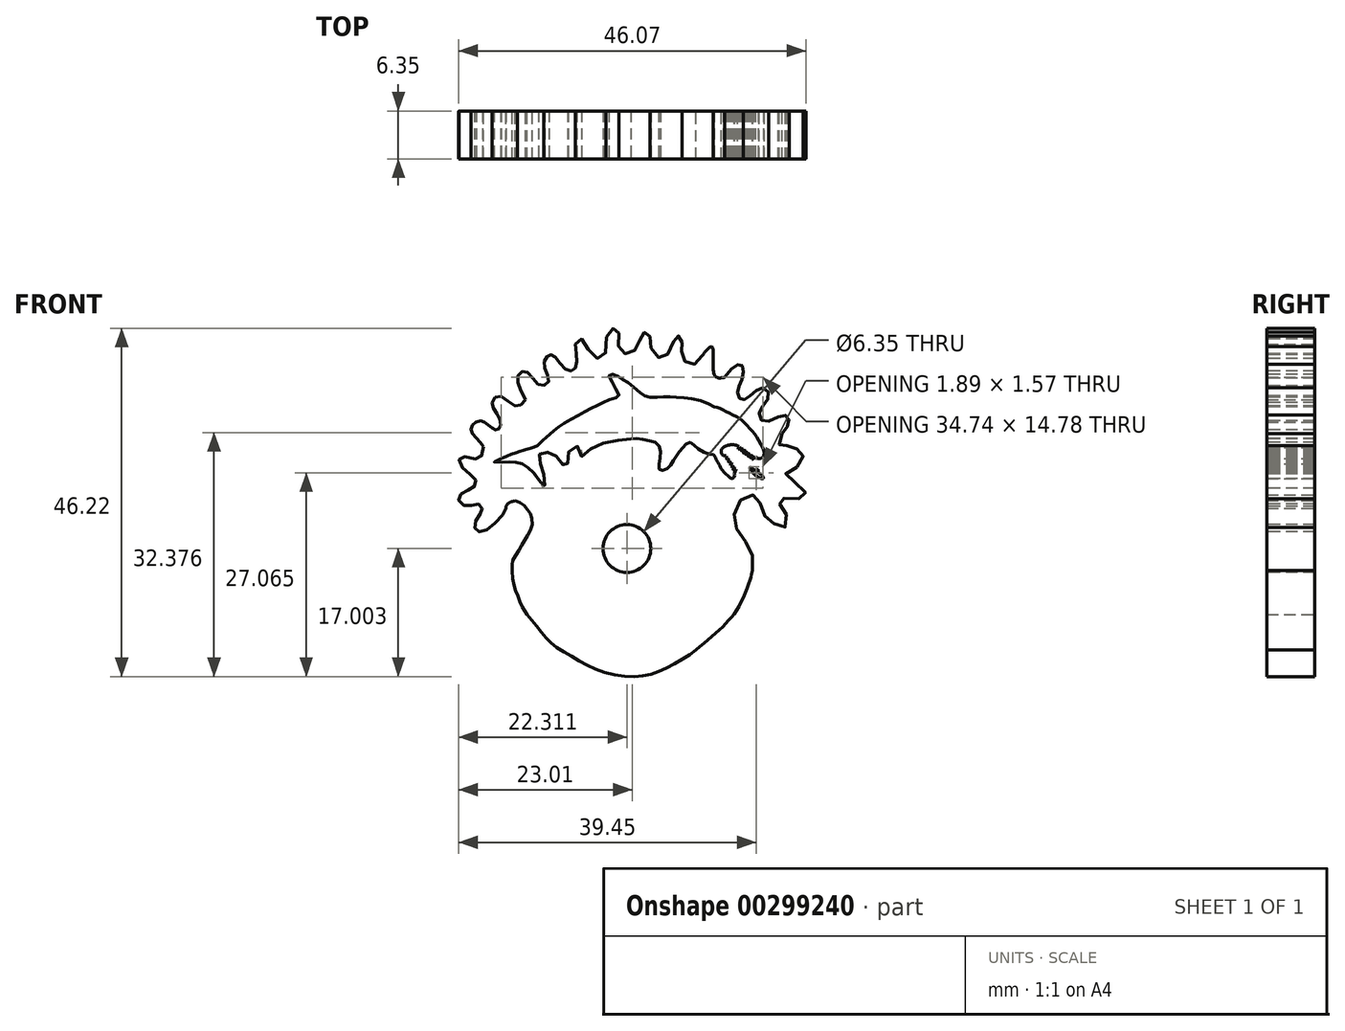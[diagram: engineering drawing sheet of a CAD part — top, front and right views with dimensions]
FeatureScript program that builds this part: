
annotation { "Feature Type Name" : "Feature", "Feature Type Description" : "" }
export const myFeature = defineFeature(function(context is Context, id is Id, definition is map)
    precondition{}
    {
        {
            var Q0;
            Q0=qCreatedBy(makeId("Front.planeOp"),FACE);
            var sketch = newSketch(context, id + "F0", { "sketchPlane" : qUnion([Q0])});
            skFitSpline(sketch, "E0", {"points": [v(11, 24.03) * mm, v(11.52, 23.48) * mm, v(10.3, 21.75) * mm, v(8.26, 20.34) * mm, v(7.4, 20.86) * mm, v(7.8, 22.28) * mm, v(8.41, 23.3) * mm, v(7.92, 24.03) * mm, v(6.5, 23.75) * mm, v(5.3, 24.5) * mm, v(5.83, 25.57) * mm, v(7.28, 26.28) * mm, v(7.5, 27.35) * mm, v(5.74, 28.86) * mm, v(5.55, 30.28) * mm, v(7.92, 30.06) * mm, v(8.54, 31.66) * mm], "startDerivative": vector(16.93, -10.31) * mm, "endDerivative": vector(2, 32.5) * mm});
            skFitSpline(sketch, "E1", {"points": [v(8.54, 31.66) * mm, v(7.8, 32.56) * mm, v(7, 33.54) * mm, v(6.98, 34.3) * mm, v(7.53, 34.9) * mm, v(8.3, 35.06) * mm, v(8.96, 34.71) * mm, v(9.68, 34.15) * mm, v(10.2, 33.88) * mm, v(10.66, 34.04) * mm, v(10.83, 34.97) * mm, v(10.2, 36.28) * mm, v(9.74, 37.52) * mm, v(10.7, 38.41) * mm, v(12.86, 37.06) * mm, v(14.16, 37.9) * mm], "startDerivative": vector(-9.67, 12.76) * mm, "endDerivative": vector(14.8, 17.95) * mm});
            skFitSpline(sketch, "E2", {"points": [v(14.16, 37.9) * mm, v(13.13, 40.99) * mm, v(14.16, 41.64) * mm, v(16.01, 39.83) * mm, v(17.22, 40.36) * mm, v(16.59, 42.52) * mm, v(17.2, 43.78) * mm, v(18.04, 43.6) * mm, v(19.74, 41.75) * mm, v(20.8, 42.22) * mm, v(20.84, 44.36) * mm, v(20.78, 45.23) * mm], "startDerivative": vector(-15.04, 27.44) * mm, "endDerivative": vector(-0.2, 11.21) * mm});
            skFitSpline(sketch, "E3", {"points": [v(20.78, 45.23) * mm, v(21.36, 45.98) * mm, v(22.11, 45.23) * mm, v(23.31, 43.54) * mm, v(24.6, 43.61) * mm, v(24.82, 46) * mm, v(25.63, 47.3) * mm, v(26.41, 47.15) * mm, v(26.46, 45.86) * mm, v(26.73, 44.34) * mm, v(27.95, 44.03) * mm, v(28.88, 44.76) * mm, v(29.34, 46) * mm, v(29.9, 46.84) * mm, v(30.54, 46.66) * mm, v(30.61, 45.52) * mm, v(31.15, 44.1) * mm, v(32.4, 43.37) * mm, v(33.45, 44.78) * mm, v(34.06, 46.15) * mm, v(34.45, 46.35) * mm, v(34.84, 46) * mm, v(34.89, 44.98) * mm, v(34.86, 44.15) * mm, v(35.33, 42.93) * mm, v(36.5, 42.59) * mm, v(37.48, 43.56) * mm, v(38.35, 44.66) * mm, v(38.9, 44.9) * mm, v(39.04, 44.37) * mm, v(39.04, 43.17) * mm, v(39.33, 40.97) * mm, v(40.58, 40.88) * mm], "startDerivative": vector(19.32, 38.87) * mm, "endDerivative": vector(46, 9.23) * mm});
            skFitSpline(sketch, "E4", {"points": [v(11, 24.03) * mm, v(11.96, 24.55) * mm, v(12.84, 24.45) * mm, v(13.82, 24.03) * mm, v(14.5, 23.15) * mm, v(14.92, 22.43) * mm, v(15, 21.06) * mm, v(14.37, 19.82) * mm, v(13.78, 18.81) * mm, v(13.1, 17.6) * mm, v(12.45, 16.53) * mm, v(12.35, 15.52) * mm, v(12.54, 13.53) * mm, v(12.94, 12.33) * mm, v(13.43, 11.02) * mm, v(13.91, 10.04) * mm, v(14.37, 9.36) * mm], "startDerivative": vector(16, 11.36) * mm, "endDerivative": vector(8.86, -12.58) * mm});
            skFitSpline(sketch, "E5", {"points": [v(14.37, 9.36) * mm, v(15.45, 8) * mm, v(16.7, 6.52) * mm, v(17.85, 5.32) * mm, v(19.75, 4.12) * mm, v(22.05, 2.83) * mm, v(24.71, 1.68) * mm, v(28.03, 1.14) * mm, v(30.47, 1.39) * mm, v(32.53, 2.14) * mm, v(35, 3.46) * mm, v(36.75, 4.66) * mm], "startDerivative": vector(13.43, -17) * mm, "endDerivative": vector(19.02, 13.7) * mm});
            skFitSpline(sketch, "E6", {"points": [v(36.75, 4.66) * mm, v(40.37, 7.83) * mm, v(42.57, 10.68) * mm, v(44.05, 14.29) * mm, v(44.25, 15.2) * mm], "startDerivative": vector(12.48, 10.37) * mm, "endDerivative": vector(0.83, 5.42) * mm});
            skFitSpline(sketch, "E7", {"points": [v(44.25, 15.2) * mm, v(44.25, 17.1) * mm, v(43.56, 18.76) * mm, v(42.32, 20.47) * mm, v(41.86, 22.06) * mm, v(42.24, 24.11) * mm, v(43.64, 25.08) * mm, v(44.73, 25.16) * mm, v(45.27, 24.07) * mm, v(45.81, 22.6) * mm, v(46.62, 21.7) * mm, v(47.71, 21.2) * mm, v(48.64, 21.01) * mm, v(48.8, 22.37) * mm, v(48.3, 23.6) * mm, v(47.71, 24.38) * mm, v(48.21, 24.77) * mm, v(49.84, 24.77) * mm, v(51.24, 24.97) * mm, v(51.16, 25.82) * mm, v(49.5, 27.21) * mm, v(48.64, 28) * mm, v(49.46, 28.5) * mm, v(50.66, 29.54) * mm, v(51, 30.55) * mm, v(50.46, 31.25) * mm, v(49.53, 31.56) * mm, v(48.68, 31.79) * mm, v(47.98, 31.56) * mm, v(47.83, 32.45) * mm, v(48.21, 33.38) * mm], "startDerivative": vector(3.57, 47.56) * mm, "endDerivative": vector(16.5, 27.7) * mm});
            skFitSpline(sketch, "E8", {"points": [v(48.21, 33.38) * mm, v(49.08, 34.78) * mm, v(48.9, 35.67) * mm, v(47.95, 35.76) * mm, v(45.92, 34.93) * mm, v(45.15, 35.88) * mm, v(45.8, 37.2) * mm, v(46.44, 38.47) * mm, v(45.82, 39.48) * mm, v(44.56, 39) * mm, v(43.55, 38.1) * mm, v(42.78, 37.91) * mm, v(42.28, 38.56) * mm, v(42.4, 39.45) * mm, v(42.87, 40.62) * mm, v(43.05, 41.94) * mm, v(42.75, 42.53) * mm, v(42.1, 42.47) * mm, v(40.58, 40.88) * mm], "startDerivative": vector(17.57, 21.46) * mm, "endDerivative": vector(-21.19, -26.63) * mm});
            skFitSpline(sketch, "E9", {"points": [v(11.52, 23.48) * mm, v(11.6, 23.82) * mm, v(11.86, 24.13) * mm, v(12.22, 24.33) * mm, v(12.75, 24.48) * mm], "startDerivative": vector(0.23, 1.54) * mm, "endDerivative": vector(1.96, 0.47) * mm});
            skFitSpline(sketch, "E10", {"points": [v(37.6, 43.73) * mm, v(37.8, 44.1) * mm, v(37.98, 44.4) * mm, v(38.28, 44.73) * mm, v(38.64, 44.95) * mm, v(38.94, 45) * mm, v(39.14, 44.72) * mm, v(39.15, 44.16) * mm, v(39.04, 43.32) * mm], "startDerivative": vector(1.68, 3.15) * mm, "endDerivative": vector(-0.67, -5.1) * mm});
            skSolve(sketch);
        }
        {
            var Q0;
            Q0=makeQuery(id+"F0.imprint","IMPRINT",FACE,{"disambiguationData":[TD([[makeQuery(id+"F0.imprint","IMPRINT",EDGE,{"derivedFrom":sQuery(id+"F0.wireOp",EDGE,"E0")}),-1.0]])]});
            extrude(context, id + "F1", {"entities" : qUnion([Q0]), "depth" : 6.35 * mm});
        }
        {
            var Q0;
            Q0=makeQuery(id+"F1.opExtrude","CAP_FACE",FACE,{"disambiguationData":[OSD([sQuery(id+"F0.wireOp",EDGE,"E0"),sQuery(id+"F0.wireOp",EDGE,"E1"),sQuery(id+"F0.wireOp",EDGE,"E2"),sQuery(id+"F0.wireOp",EDGE,"E3"),sQuery(id+"F0.wireOp",EDGE,"E4"),sQuery(id+"F0.wireOp",EDGE,"E5"),sQuery(id+"F0.wireOp",EDGE,"E6"),sQuery(id+"F0.wireOp",EDGE,"E7"),sQuery(id+"F0.wireOp",EDGE,"E8")])],"isStart":false});
            var sketch = newSketch(context, id + "F2", { "sketchPlane" : qUnion([Q0])});
            skFitSpline(sketch, "E11", {"points": [v(10.92, 30.08) * mm, v(10.63, 30) * mm, v(10.4, 29.82) * mm, v(10.16, 29.68) * mm, v(9.97, 29.6) * mm, v(10.25, 29.54) * mm, v(10.58, 29.58) * mm, v(10.89, 29.58) * mm, v(11.18, 29.65) * mm, v(11.47, 29.65) * mm, v(11.84, 29.67) * mm, v(12.08, 29.67) * mm, v(12.3, 29.67) * mm, v(12.46, 29.67) * mm, v(12.65, 29.67) * mm, v(12.9, 29.6) * mm, v(13, 29.54) * mm, v(13.25, 29.53) * mm, v(13.46, 29.46) * mm, v(13.61, 29.39) * mm, v(13.79, 29.34) * mm, v(13.98, 29.22) * mm, v(14.25, 29.08) * mm, v(14.34, 29) * mm, v(14.55, 28.82) * mm, v(14.74, 28.65) * mm, v(14.96, 28.46) * mm, v(15.22, 28.25) * mm, v(15.62, 27.71) * mm, v(15.93, 27.25) * mm, v(16.3, 26.71) * mm, v(16.53, 26.13) * mm, v(16.65, 26.3) * mm, v(16.65, 26.89) * mm, v(16.62, 27.42) * mm, v(16.57, 27.96) * mm, v(16.45, 28.72) * mm, v(16.22, 29.23) * mm, v(16.05, 29.61) * mm, v(15.9, 30.1) * mm, v(15.95, 30.48) * mm, v(16.17, 30.84) * mm, v(16.5, 30.93) * mm, v(16.86, 30.93) * mm, v(17.22, 30.93) * mm, v(17.59, 30.9) * mm, v(18.02, 30.56) * mm, v(18.41, 30.24) * mm, v(18.81, 29.84) * mm, v(19.09, 29.29) * mm, v(19.23, 29.29) * mm, v(19.36, 29.29) * mm, v(19.57, 29.37) * mm, v(19.67, 29.37) * mm, v(19.76, 29.46) * mm, v(19.76, 29.67) * mm, v(19.78, 30.65) * mm, v(19.97, 31.08) * mm, v(20.4, 31.32) * mm, v(20.73, 31.62) * mm, v(21.35, 31.67) * mm, v(21.6, 31.1) * mm, v(21.64, 30.3) * mm, v(22.1, 30.77) * mm, v(22.82, 31.36) * mm, v(23.6, 31.84) * mm, v(24.39, 32.12) * mm, v(25.54, 32.34) * mm, v(26.46, 32.5) * mm, v(27.3, 32.6) * mm, v(28.13, 32.7) * mm], "startDerivative": vector(-24.75, -4.73) * mm, "endDerivative": vector(40, 5.16) * mm});
            skFitSpline(sketch, "E12", {"points": [v(10.92, 30.08) * mm, v(11.43, 30.3) * mm, v(12.7, 30.81) * mm, v(13.7, 31.1) * mm, v(14.35, 31.33) * mm, v(15.48, 31.66) * mm, v(16.04, 32.15) * mm, v(16.96, 32.95) * mm, v(18.4, 34.16) * mm, v(21.6, 36.09) * mm, v(24.46, 37.53) * mm], "startDerivative": vector(6.76, 4.38) * mm, "endDerivative": vector(18.3, 8.91) * mm});
            skFitSpline(sketch, "E13", {"points": [v(24.46, 37.53) * mm, v(25.3, 37.9) * mm, v(26.23, 38.16) * mm, v(26.54, 38.4) * mm, v(26.16, 39.24) * mm, v(25.6, 40.4) * mm, v(25.23, 41.14) * mm, v(25.58, 41.28) * mm, v(26.23, 41.12) * mm, v(26.78, 40.74) * mm, v(27.5, 40.35) * mm, v(28.33, 39.73) * mm, v(29.34, 38.84) * mm, v(29.96, 38.4) * mm, v(30.58, 38.24) * mm, v(31.56, 38.22) * mm, v(32.45, 38.25) * mm, v(33.44, 38.25) * mm, v(34.26, 38.18) * mm, v(35.48, 38.1) * mm, v(36.95, 37.9) * mm, v(38.6, 37.29) * mm, v(39.14, 36.96) * mm], "startDerivative": vector(17.5, 9.22) * mm, "endDerivative": vector(11.79, -8.04) * mm});
            skFitSpline(sketch, "E14", {"points": [v(28.13, 32.7) * mm, v(29.12, 32.7) * mm, v(30.5, 32.46) * mm, v(31.45, 32.15) * mm, v(32, 31.47) * mm, v(32.03, 30.25) * mm, v(31.83, 29.13) * mm, v(31.9, 28.62) * mm, v(32.38, 28.53) * mm, v(33.11, 28.88) * mm, v(33.56, 29.5) * mm, v(34.02, 30.25) * mm, v(34.55, 30.97) * mm, v(35.13, 31.66) * mm, v(35.56, 32.07) * mm, v(36.06, 32.2) * mm, v(36.68, 31.66) * mm, v(37.7, 30.99) * mm, v(38.71, 30.6) * mm, v(39.08, 30.6) * mm], "startDerivative": vector(16.41, 0.56) * mm, "endDerivative": vector(9.35, 1.15) * mm});
            skFitSpline(sketch, "E15", {"points": [v(39.08, 30.6) * mm, v(39.7, 29.53) * mm, v(40.3, 28.5) * mm, v(41.08, 27.7) * mm, v(41.55, 27.43) * mm, v(41.87, 27.78) * mm, v(41.48, 28.86) * mm, v(40.74, 30.06) * mm, v(40.1, 30.98) * mm, v(40.56, 31.66) * mm, v(41.68, 31.9) * mm, v(42.54, 31.66) * mm, v(43.78, 30.89) * mm, v(44.59, 30.34) * mm, v(45.19, 30.06) * mm, v(45.83, 30.6) * mm, v(45.23, 32.25) * mm, v(44.52, 33.38) * mm, v(43.69, 34.3) * mm, v(43, 35.04) * mm, v(41.96, 35.73) * mm, v(40.9, 36.26) * mm, v(39.9, 36.77) * mm, v(39.14, 36.96) * mm], "startDerivative": vector(13.65, -22.59) * mm, "endDerivative": vector(-20.03, 3.48) * mm});
            skSolve(sketch);
        }
        {
            var Q0;
            Q0=makeQuery(id+"F2.imprint","IMPRINT",FACE,{"disambiguationData":[TD([[makeQuery(id+"F2.imprint","IMPRINT",EDGE,{"derivedFrom":sQuery(id+"F2.wireOp",EDGE,"E11")}),1.0]])]});
            extrude(context, id + "F3", {"entities" : qUnion([Q0]), "operationType" : NewBodyOperationType.REMOVE, "oppositeDirection" : true, "depth" : 25.4 * mm});
        }
        {
            var Q0;
            Q0=makeQuery(id+"F1.opExtrude","CAP_FACE",FACE,{"disambiguationData":[OSD([sQuery(id+"F0.wireOp",EDGE,"E0"),sQuery(id+"F0.wireOp",EDGE,"E1"),sQuery(id+"F0.wireOp",EDGE,"E2"),sQuery(id+"F0.wireOp",EDGE,"E3"),sQuery(id+"F0.wireOp",EDGE,"E4"),sQuery(id+"F0.wireOp",EDGE,"E5"),sQuery(id+"F0.wireOp",EDGE,"E6"),sQuery(id+"F0.wireOp",EDGE,"E7"),sQuery(id+"F0.wireOp",EDGE,"E8")])],"isStart":false});
            var sketch = newSketch(context, id + "F4", { "sketchPlane" : qUnion([Q0])});
            skLineSegment(sketch, "E16", {"start": v(40.36, 30.5) * mm, "end": v(40.75, 30.5) * mm});
            skLineSegment(sketch, "E17", {"start": v(40.75, 30.5) * mm, "end": v(40.62, 30.2) * mm});
            skLineSegment(sketch, "E18", {"start": v(40.62, 30.2) * mm, "end": v(41.01, 30.2) * mm});
            skLineSegment(sketch, "E19", {"start": v(41.01, 30.2) * mm, "end": v(40.91, 29.83) * mm});
            skLineSegment(sketch, "E20", {"start": v(40.91, 29.83) * mm, "end": v(41.29, 29.83) * mm});
            skLineSegment(sketch, "E21", {"start": v(41.29, 29.83) * mm, "end": v(41.17, 29.42) * mm});
            skLineSegment(sketch, "E22", {"start": v(41.17, 29.42) * mm, "end": v(41.51, 29.54) * mm});
            skLineSegment(sketch, "E23", {"start": v(41.51, 29.54) * mm, "end": v(41.33, 29.12) * mm});
            skLineSegment(sketch, "E24", {"start": v(41.33, 29.12) * mm, "end": v(41.67, 29.23) * mm});
            skLineSegment(sketch, "E25", {"start": v(41.67, 29.23) * mm, "end": v(41.5, 28.82) * mm});
            skLineSegment(sketch, "E26", {"start": v(41.5, 28.82) * mm, "end": v(41.92, 28.98) * mm});
            skLineSegment(sketch, "E27", {"start": v(41.92, 28.98) * mm, "end": v(41.67, 28.5) * mm});
            skLineSegment(sketch, "E28", {"start": v(41.67, 28.5) * mm, "end": v(42.1, 28.68) * mm});
            skLineSegment(sketch, "E29", {"start": v(42.1, 28.68) * mm, "end": v(41.84, 28.08) * mm});
            skLineSegment(sketch, "E30", {"start": v(42.47, 31.7) * mm, "end": v(42.32, 31.32) * mm});
            skLineSegment(sketch, "E31", {"start": v(42.32, 31.32) * mm, "end": v(42.78, 31.53) * mm});
            skLineSegment(sketch, "E32", {"start": v(42.78, 31.53) * mm, "end": v(42.62, 31.16) * mm});
            skLineSegment(sketch, "E33", {"start": v(42.62, 31.16) * mm, "end": v(43.02, 31.39) * mm});
            skLineSegment(sketch, "E34", {"start": v(43.02, 31.39) * mm, "end": v(42.85, 30.88) * mm});
            skLineSegment(sketch, "E35", {"start": v(42.85, 30.88) * mm, "end": v(43.4, 31.15) * mm});
            skLineSegment(sketch, "E36", {"start": v(43.4, 31.15) * mm, "end": v(43.19, 30.6) * mm});
            skLineSegment(sketch, "E37", {"start": v(43.19, 30.6) * mm, "end": v(43.7, 30.94) * mm});
            skLineSegment(sketch, "E38", {"start": v(43.7, 30.94) * mm, "end": v(43.48, 30.42) * mm});
            skLineSegment(sketch, "E39", {"start": v(43.48, 30.42) * mm, "end": v(44.02, 30.73) * mm});
            skLineSegment(sketch, "E40", {"start": v(44.02, 30.73) * mm, "end": v(43.78, 30.17) * mm});
            skLineSegment(sketch, "E41", {"start": v(43.78, 30.17) * mm, "end": v(44.36, 30.5) * mm});
            skLineSegment(sketch, "E42", {"start": v(44.36, 30.5) * mm, "end": v(44.15, 29.95) * mm});
            skLineSegment(sketch, "E43", {"start": v(44.15, 29.95) * mm, "end": v(44.64, 30.3) * mm});
            skSolve(sketch);
        }
        {
            var Q0;
            {var subQ0=sQuery(id+"F4.wireOp",EDGE,"E24");Q0=makeQuery(id+"F4.imprint","IMPRINT",FACE,{"disambiguationData":[TD([[makeQuery(id+"F4.imprint","IMPRINT",EDGE,{"derivedFrom":subQ0}),-1.0]])]});}
            var Q1;
            {var subQ0=sQuery(id+"F4.wireOp",EDGE,"E22");Q1=makeQuery(id+"F4.imprint","IMPRINT",FACE,{"disambiguationData":[TD([[makeQuery(id+"F4.imprint","IMPRINT",EDGE,{"derivedFrom":subQ0}),-1.0]])]});}
            var Q2;
            {var subQ0=sQuery(id+"F4.wireOp",EDGE,"E20");Q2=makeQuery(id+"F4.imprint","IMPRINT",FACE,{"disambiguationData":[TD([[makeQuery(id+"F4.imprint","IMPRINT",EDGE,{"derivedFrom":subQ0}),-1.0]])]});}
            var Q3;
            {var subQ0=sQuery(id+"F4.wireOp",EDGE,"E18");Q3=makeQuery(id+"F4.imprint","IMPRINT",FACE,{"disambiguationData":[TD([[makeQuery(id+"F4.imprint","IMPRINT",EDGE,{"derivedFrom":subQ0}),-1.0]])]});}
            var Q4;
            {var subQ0=sQuery(id+"F4.wireOp",EDGE,"E16");Q4=makeQuery(id+"F4.imprint","IMPRINT",FACE,{"disambiguationData":[TD([[makeQuery(id+"F4.imprint","IMPRINT",EDGE,{"derivedFrom":subQ0}),-1.0]])]});}
            var Q5;
            {var subQ0=sQuery(id+"F4.wireOp",EDGE,"E26");Q5=makeQuery(id+"F4.imprint","IMPRINT",FACE,{"disambiguationData":[TD([[makeQuery(id+"F4.imprint","IMPRINT",EDGE,{"derivedFrom":subQ0}),-1.0]])]});}
            var Q6;
            {var subQ0=sQuery(id+"F4.wireOp",EDGE,"E28");Q6=makeQuery(id+"F4.imprint","IMPRINT",FACE,{"disambiguationData":[TD([[makeQuery(id+"F4.imprint","IMPRINT",EDGE,{"derivedFrom":subQ0}),-1.0]])]});}
            var Q7;
            {var subQ0=sQuery(id+"F4.wireOp",EDGE,"E42");Q7=makeQuery(id+"F4.imprint","IMPRINT",FACE,{"disambiguationData":[TD([[makeQuery(id+"F4.imprint","IMPRINT",EDGE,{"derivedFrom":subQ0}),1.0]])]});}
            var Q8;
            {var subQ0=sQuery(id+"F4.wireOp",EDGE,"E40");Q8=makeQuery(id+"F4.imprint","IMPRINT",FACE,{"disambiguationData":[TD([[makeQuery(id+"F4.imprint","IMPRINT",EDGE,{"derivedFrom":subQ0}),1.0]])]});}
            var Q9;
            {var subQ0=sQuery(id+"F4.wireOp",EDGE,"E38");Q9=makeQuery(id+"F4.imprint","IMPRINT",FACE,{"disambiguationData":[TD([[makeQuery(id+"F4.imprint","IMPRINT",EDGE,{"derivedFrom":subQ0}),1.0]])]});}
            var Q10;
            {var subQ0=sQuery(id+"F4.wireOp",EDGE,"E36");Q10=makeQuery(id+"F4.imprint","IMPRINT",FACE,{"disambiguationData":[TD([[makeQuery(id+"F4.imprint","IMPRINT",EDGE,{"derivedFrom":subQ0}),1.0]])]});}
            var Q11;
            {var subQ0=sQuery(id+"F4.wireOp",EDGE,"E34");Q11=makeQuery(id+"F4.imprint","IMPRINT",FACE,{"disambiguationData":[TD([[makeQuery(id+"F4.imprint","IMPRINT",EDGE,{"derivedFrom":subQ0}),1.0]])]});}
            var Q12;
            {var subQ0=sQuery(id+"F4.wireOp",EDGE,"E32");Q12=makeQuery(id+"F4.imprint","IMPRINT",FACE,{"disambiguationData":[TD([[makeQuery(id+"F4.imprint","IMPRINT",EDGE,{"derivedFrom":subQ0}),1.0]])]});}
            var Q13;
            {var subQ0=sQuery(id+"F4.wireOp",EDGE,"E30");Q13=makeQuery(id+"F4.imprint","IMPRINT",FACE,{"disambiguationData":[TD([[makeQuery(id+"F4.imprint","IMPRINT",EDGE,{"derivedFrom":subQ0}),1.0]])]});}
            extrude(context, id + "F5", {"entities" : qUnion([Q0, Q1, Q2, Q3, Q4, Q5, Q6, Q7, Q8, Q9, Q10, Q11, Q12, Q13]), "operationType" : NewBodyOperationType.REMOVE, "oppositeDirection" : true, "depth" : 25.4 * mm});
        }
        {
            var Q0;
            Q0=makeQuery(id+"F1.opExtrude","CAP_FACE",FACE,{"disambiguationData":[OSD([sQuery(id+"F0.wireOp",EDGE,"E0"),sQuery(id+"F0.wireOp",EDGE,"E1"),sQuery(id+"F0.wireOp",EDGE,"E2"),sQuery(id+"F0.wireOp",EDGE,"E3"),sQuery(id+"F0.wireOp",EDGE,"E4"),sQuery(id+"F0.wireOp",EDGE,"E5"),sQuery(id+"F0.wireOp",EDGE,"E6"),sQuery(id+"F0.wireOp",EDGE,"E7"),sQuery(id+"F0.wireOp",EDGE,"E8")])],"isStart":false});
            var sketch = newSketch(context, id + "F6", { "sketchPlane" : qUnion([Q0])});
            skCircle(sketch, "E44", {"center": v(27.6, 18.14) * mm, "radius": 3.18 * mm});
            skSolve(sketch);
        }
        {
            var Q0;
            Q0=makeQuery(id+"F6.imprint","IMPRINT",FACE,{"disambiguationData":[TD([[makeQuery(id+"F6.imprint","IMPRINT",EDGE,{"derivedFrom":sQuery(id+"F6.wireOp",EDGE,"E44")}),1.0]])]});
            extrude(context, id + "F7", {"entities" : qUnion([Q0]), "operationType" : NewBodyOperationType.REMOVE, "oppositeDirection" : true, "depth" : 25.4 * mm});
        }
        {
            var Q0;
            {var subQ3=sQuery(id+"F0.wireOp",EDGE,"E9");Q0=makeQuery(id+"F0.imprint","IMPRINT",FACE,{"disambiguationData":[TD([[makeQuery(id+"F0.imprint","IMPRINT",EDGE,{"derivedFrom":subQ3}),1.0]])]});}
            extrude(context, id + "F8", {"entities" : qUnion([Q0]), "operationType" : NewBodyOperationType.ADD, "depth" : 6.35 * mm});
        }
        {
            var Q0;
            {var subQ0=sQuery(id+"F0.wireOp",EDGE,"E4");var subQ1=sQuery(id+"F0.wireOp",EDGE,"E0");Q0=makeQuery(id+"F8.boolean.opBoolean","MERGE",FACE,{"derivedFrom":[makeQuery(id+"F1.opExtrude","CAP_FACE",FACE,{"disambiguationData":[OSD([subQ1,sQuery(id+"F0.wireOp",EDGE,"E1"),sQuery(id+"F0.wireOp",EDGE,"E2"),sQuery(id+"F0.wireOp",EDGE,"E3"),subQ0,sQuery(id+"F0.wireOp",EDGE,"E5"),sQuery(id+"F0.wireOp",EDGE,"E6"),sQuery(id+"F0.wireOp",EDGE,"E7"),sQuery(id+"F0.wireOp",EDGE,"E8")])],"isStart":false}),makeQuery(id+"F8.opExtrude","CAP_FACE",FACE,{"disambiguationData":[OSD([subQ1,subQ0,sQuery(id+"F0.wireOp",EDGE,"E9")])],"isStart":false})]});}
            var sketch = newSketch(context, id + "F9", { "sketchPlane" : qUnion([Q0])});
            skLineSegment(sketch, "E45", {"start": v(44.11, 29) * mm, "end": v(43.79, 28.69) * mm});
            skLineSegment(sketch, "E46", {"start": v(43.79, 28.69) * mm, "end": v(44.11, 28.56) * mm});
            skLineSegment(sketch, "E47", {"start": v(44.11, 29) * mm, "end": v(44.23, 28.66) * mm});
            skFitSpline(sketch, "E48", {"points": [v(44.11, 28.56) * mm, v(44.29, 28.2) * mm, v(44.52, 27.99) * mm, v(44.81, 27.75) * mm, v(45.24, 27.52) * mm, v(45.7, 27.43) * mm, v(45.62, 27.7) * mm, v(45.38, 27.99) * mm, v(44.95, 28.27) * mm, v(44.57, 28.56) * mm, v(44.23, 28.66) * mm], "startDerivative": vector(1.57, -3.84) * mm, "endDerivative": vector(-3.65, 0.79) * mm});
            skFitSpline(sketch, "E49", {"points": [v(44.65, 28.5) * mm, v(45, 28.59) * mm, v(45, 28.23) * mm], "startDerivative": vector(0.89, 0.4) * mm, "endDerivative": vector(-0.16, -0.93) * mm});
            skSolve(sketch);
        }
        {
            var Q0;
            Q0 = qSketchRegion(id + "F9", true);
            extrude(context, id + "F10", {"entities" : qUnion([Q0]), "operationType" : NewBodyOperationType.REMOVE, "oppositeDirection" : true, "depth" : 25.4 * mm});
        }
    });
